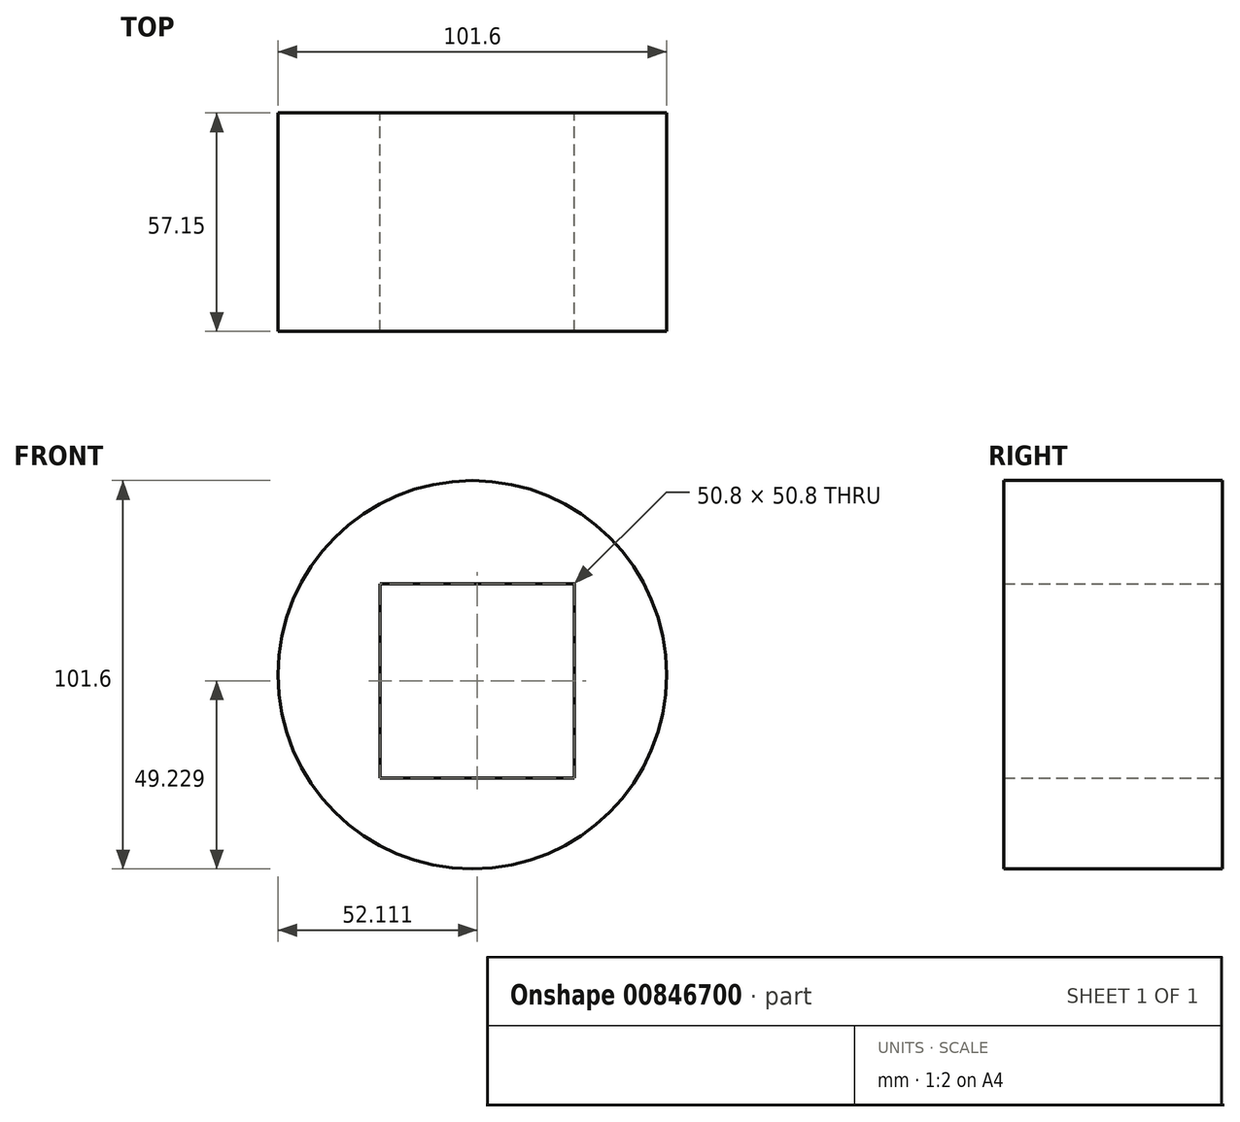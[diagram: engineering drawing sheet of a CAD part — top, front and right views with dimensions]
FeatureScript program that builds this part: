
annotation { "Feature Type Name" : "Feature", "Feature Type Description" : "" }
export const myFeature = defineFeature(function(context is Context, id is Id, definition is map)
    precondition{}
    {
        {
            var Q0;
            Q0=qCreatedBy(makeId("Front.planeOp"),FACE);
            var sketch = newSketch(context, id + "F0", { "sketchPlane" : qUnion([Q0])});
            skCircle(sketch, "E0", {"center": v(0, 0) * mm, "radius": 63.5 * mm});
            skCircle(sketch, "E1", {"center": v(0, 0) * mm, "radius": 50.8 * mm});
            skPoint(sketch, "E2", {"position": v(0, 50.8) * mm});
            skArc(sketch, "E3", {"start": v(5.33, 50.52) * mm, "mid": v(0.55, 55.47) * mm, "end": v(-4.33, 50.62) * mm});
            skArc(sketch, "E4", {"start": v(50.38, -6.51) * mm, "mid": v(55.37, -1.85) * mm, "end": v(50.7, 3.13) * mm});
            skPoint(sketch, "E5", {"position": v(0, -50.8) * mm});
            skArc(sketch, "E6", {"start": v(-5.2, -50.53) * mm, "mid": v(-0.41, -55.4) * mm, "end": v(4.45, -50.6) * mm});
            skPoint(sketch, "E7", {"position": v(-50.62, 4.33) * mm});
            skArc(sketch, "E8", {"start": v(-49.88, 9.6) * mm, "mid": v(-55.15, 5.26) * mm, "end": v(-50.8, 0) * mm});
            skLineSegment(sketch, "E9.bottom", {"start": v(-24.09, -26.97) * mm, "end": v(26.71, -26.97) * mm});
            skLineSegment(sketch, "E9.top", {"start": v(-24.09, 23.83) * mm, "end": v(26.71, 23.83) * mm});
            skLineSegment(sketch, "E9.left", {"start": v(-24.09, -26.97) * mm, "end": v(-24.09, 23.83) * mm});
            skLineSegment(sketch, "E9.right", {"start": v(26.71, -26.97) * mm, "end": v(26.71, 23.83) * mm});
            skCircle(sketch, "E10", {"center": v(0, 0) * mm, "radius": 45.8 * mm});
            skSolve(sketch);
        }
        {
            var Q0;
            Q0=makeQuery(id+"F0.imprint","IMPRINT",FACE,{"disambiguationData":[TD([[makeQuery(id+"F0.imprint","IMPRINT",EDGE,{"derivedFrom":sQuery(id+"F0.wireOp",EDGE,"E9.bottom")}),-1.0]])]});
            var Q1;
            Q1=makeQuery(id+"F0.imprint","IMPRINT",FACE,{"disambiguationData":[TD([[makeQuery(id+"F0.imprint","IMPRINT",EDGE,{"derivedFrom":sQuery(id+"F0.wireOp",EDGE,"E10")}),-1.0]])]});
            var Q2;
            Q2=sQuery(id+"F0.wireOp",EDGE,"E8");
            var Q3;
            Q3=sQuery(id+"F0.wireOp",EDGE,"E6");
            var Q4;
            Q4=sQuery(id+"F0.wireOp",EDGE,"E4");
            var Q5;
            Q5=sQuery(id+"F0.wireOp",EDGE,"E3");
            var Q6;
            Q6=sQuery(id+"F0.wireOp",EDGE,"E1");
            var Q7;
            Q7=sQuery(id+"F0.wireOp",EDGE,"E10");
            extrude(context, id + "F1", {"entities" : qUnion([Q0, Q1]), "surfaceOperationType" : NewSurfaceOperationType.ADD, "surfaceEntities" : qUnion([Q2, Q3, Q4, Q5, Q6, Q7]), "depth" : 57.15 * mm, "offsetDistance" : 25.4 * mm});
        }
    });
